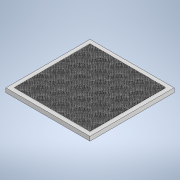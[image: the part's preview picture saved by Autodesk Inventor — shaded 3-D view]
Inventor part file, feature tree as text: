
AUTODESK INVENTOR PART (.ipt)
format: ipt  version: 2021 (Build 250183000, 183)  size: 19,249,152 bytes
history: native  units: mm
features: extrude x3, sketch x3, pattern_linear x2
ambient origin geometry x8: Origin, YZ Plane, XZ Plane, XY Plane, X Axis, Y Axis, Z Axis, Center Point
bodies: Solid1 (feature_tree)
feature tree (8):
  extrude  "Extrusion1"  Depth=200.0mm
  extrude  "Extrusion2"  Depth=180.0mm
  pattern_linear  "Rectangular Pattern1"  Spacing1=1.0mm  [1 undecoded]
  extrude  "Extrusion3"  Depth=2.0mm
  pattern_linear  "Rectangular Pattern2"  Spacing1=1.0mm  [1 undecoded]
  sketch  "Sketch1"  dims[d0=200.0mm d1=200.0mm]
  sketch  "Sketch2"  dims[d2=10.0mm d3=0.0mm d4=180.0mm]
  sketch  "Sketch3"  dims[d5=1.0mm d6=1.0mm d7=0.0mm d8=900.0mm d10=2.0mm d11=1.0mm d12=180.0mm d13=1.0mm d14=0.0mm d15=900.0mm d17=2.0mm]
note: 2 required parameter values undecoded (feature->parameter linkage not recoverable at this tier; creation-order binding heuristic only, values carry confidence <= 0.55)
